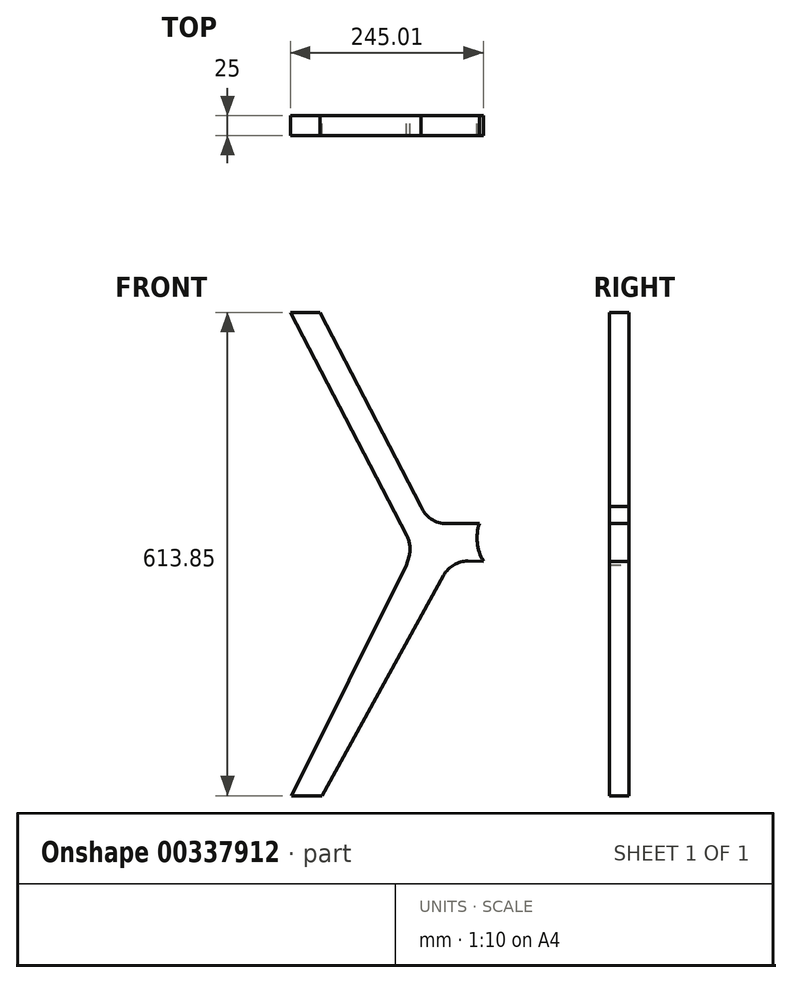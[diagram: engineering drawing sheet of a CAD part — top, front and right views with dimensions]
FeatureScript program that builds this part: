
annotation { "Feature Type Name" : "Feature", "Feature Type Description" : "" }
export const myFeature = defineFeature(function(context is Context, id is Id, definition is map)
    precondition{}
    {
        {
            var Q0;
            Q0=qCreatedBy(makeId("Front.planeOp"),FACE);
            var sketch = newSketch(context, id + "F0", { "sketchPlane" : qUnion([Q0])});
            skLineSegment(sketch, "E0.top", {"start": v(348.78, -158.15) * mm, "end": v(325.9, -158.15) * mm});
            skLineSegment(sketch, "E0.left", {"start": v(348.78, 219.3) * mm, "end": v(348.78, -158.15) * mm});
            skPoint(sketch, "E0.middle", {"position": v(0, 0) * mm});
            skLineSegment(sketch, "E1", {"start": v(-310.5, 344.83) * mm, "end": v(-363.6, 344.83) * mm});
            skFitSpline(sketch, "E2", {"points": [v(-350.67, 344.83) * mm, v(347.35, 254.73) * mm, v(923.32, -91.46) * mm, v(911.37, -154.4) * mm, v(869.65, -185.3) * mm], "startDerivative": vector(1663.46, -7.35) * mm, "endDerivative": vector(-3077.7, -870.32) * mm});
            skLineSegment(sketch, "E3", {"start": v(348.78, 219.3) * mm, "end": v(347.5, 251.23) * mm});
            skLineSegment(sketch, "E4.0", {"start": v(280.23, 190.93) * mm, "end": v(-218.88, 187.87) * mm});
            skPoint(sketch, "E5.newPointA", {"position": v(-350, 535) * mm});
            skLineSegment(sketch, "E6", {"start": v(-318.8, 187.25) * mm, "end": v(-458.7, 455.7) * mm});
            skLineSegment(sketch, "E7", {"start": v(-311.32, 135.27) * mm, "end": v(-457.28, -158.15) * mm});
            skLineSegment(sketch, "E8", {"start": v(-418.69, -158.15) * mm, "end": v(-457.28, -158.15) * mm});
            skArc(sketch, "E9", {"start": v(-218.88, 187.87) * mm, "mid": v(-221.35, 163.28) * mm, "end": v(-213.7, 139.78) * mm});
            skLineSegment(sketch, "E10.trimOffspring", {"start": v(326.04, -158.15) * mm, "end": v(326.04, -159.41) * mm});
            skLineSegment(sketch, "E11", {"start": v(-318.8, 187.25) * mm, "end": v(-310.8, 171.92) * mm});
            skLineSegment(sketch, "E12", {"start": v(-311.32, 135.27) * mm, "end": v(-308.21, 146.05) * mm});
            skArc(sketch, "E13.filletArc", {"start": v(-308.21, 146.05) * mm, "mid": v(-307.02, 159.24) * mm, "end": v(-310.8, 171.92) * mm});
            skLineSegment(sketch, "E14.filletArc", {"start": v(279.23, 184.4) * mm, "end": v(279.23, 184.4) * mm});
            skLineSegment(sketch, "E15", {"start": v(280.23, 190.93) * mm, "end": v(300.92, 190.93) * mm});
            skLineSegment(sketch, "E16.trimOffspring", {"start": v(325.9, -158.15) * mm, "end": v(326.04, -159.41) * mm});
            skLineSegment(sketch, "E17", {"start": v(-287.9, 78.75) * mm, "end": v(-418.69, -158.15) * mm});
            skArc(sketch, "E18.trimOffspring", {"start": v(299.4, 190.93) * mm, "mid": v(299.33, 190.97) * mm, "end": v(299.25, 191) * mm});
            skArc(sketch, "E19.0", {"start": v(307.52, 136.2) * mm, "mid": v(309.15, 164.16) * mm, "end": v(300.92, 190.93) * mm});
            skLineSegment(sketch, "E20", {"start": v(294.6, 136.3) * mm, "end": v(-233.24, 139.91) * mm});
            skArc(sketch, "E21.filletArc", {"start": v(314.46, 116.85) * mm, "mid": v(308.46, 130.58) * mm, "end": v(294.6, 136.3) * mm});
            skLineSegment(sketch, "E22.0", {"start": v(-292.9, 209.2) * mm, "end": v(-421.38, 455.7) * mm});
            skLineSegment(sketch, "E23", {"start": v(-194.49, 188.02) * mm, "end": v(-260.36, 187.61) * mm});
            skArc(sketch, "E24.filletArc", {"start": v(-292.9, 209.2) * mm, "mid": v(-279.92, 193.44) * mm, "end": v(-260.36, 187.61) * mm});
            skLineSegment(sketch, "E25", {"start": v(-457.28, -158.15) * mm, "end": v(348.78, -158.15) * mm, "construction": true});
            skLineSegment(sketch, "E26", {"start": v(-458.7, 455.7) * mm, "end": v(-421.38, 455.7) * mm});
            skLineSegment(sketch, "E27", {"start": v(-297.94, 60.56) * mm, "end": v(-264.12, 121.83) * mm});
            skArc(sketch, "E28.filletArc", {"start": v(-233.24, 139.91) * mm, "mid": v(-251.17, 135.12) * mm, "end": v(-264.12, 121.83) * mm});
            skLineSegment(sketch, "E29", {"start": v(314.46, 116.85) * mm, "end": v(323.78, -158.15) * mm});
            skLineSegment(sketch, "E30", {"start": v(323.78, -158.15) * mm, "end": v(348.78, -158.15) * mm});
            skLineSegment(sketch, "E31", {"start": v(300.92, 190.93) * mm, "end": v(309.64, 190.93) * mm});
            skArc(sketch, "E32.filletArc", {"start": v(309.64, 190.93) * mm, "mid": v(323.78, 196.79) * mm, "end": v(329.64, 210.93) * mm});
            skLineSegment(sketch, "E33", {"start": v(347.5, 251.23) * mm, "end": v(347.5, 286.23) * mm});
            skLineSegment(sketch, "E34", {"start": v(-363.6, 379.83) * mm, "end": v(-381.83, 379.83) * mm});
            skFitSpline(sketch, "E35", {"points": [v(-381.83, 379.83) * mm, v(347.5, 286.23) * mm, v(695.3, 144.82) * mm], "startDerivative": vector(1371.77, -108.32) * mm, "endDerivative": vector(747.87, -376.57) * mm});
            skLineSegment(sketch, "E36", {"start": v(329.64, 210.93) * mm, "end": v(329.64, 260.32) * mm});
            skLineSegment(sketch, "E37", {"start": v(347.5, 286.23) * mm, "end": v(329.64, 260.32) * mm});
            skLineSegment(sketch, "E38", {"start": v(307.52, 136.2) * mm, "end": v(294.6, 136.3) * mm});
            skSolve(sketch);
        }
        {
            var Q0;
            Q0=makeQuery(id+"F0.imprint","IMPRINT",FACE,{"disambiguationData":[TD([[makeQuery(id+"F0.imprint","IMPRINT",EDGE,{"derivedFrom":sQuery(id+"F0.wireOp",EDGE,"E6")}),-1.0]])]});
            var sketch = newSketch(context, id + "F1", { "sketchPlane" : qUnion([Q0])});
            skLineSegment(sketch, "E39.0", {"start": v(-287.9, 78.75) * mm, "end": v(-418.69, -158.15) * mm});
            skLineSegment(sketch, "E39.1", {"start": v(-311.32, 135.27) * mm, "end": v(-457.28, -158.15) * mm});
            skLineSegment(sketch, "E39.2", {"start": v(-318.8, 187.25) * mm, "end": v(-458.7, 455.7) * mm});
            skLineSegment(sketch, "E39.3", {"start": v(-292.9, 209.2) * mm, "end": v(-421.38, 455.7) * mm});
            skLineSegment(sketch, "E39.4", {"start": v(-218.88, 187.87) * mm, "end": v(-260.36, 187.61) * mm});
            skArc(sketch, "E39.5.0", {"start": v(-213.7, 139.78) * mm, "mid": v(-221.35, 163.28) * mm, "end": v(-218.88, 187.87) * mm});
            skLineSegment(sketch, "E39.5.1", {"start": v(-218.88, 187.87) * mm, "end": v(-260.36, 187.61) * mm});
            skArc(sketch, "E39.5.2", {"start": v(-260.36, 187.61) * mm, "mid": v(-279.92, 193.44) * mm, "end": v(-292.9, 209.2) * mm});
            skLineSegment(sketch, "E39.5.3", {"start": v(-292.9, 209.2) * mm, "end": v(-363.6, 344.83) * mm});
            skLineSegment(sketch, "E39.5.4", {"start": v(-363.6, 344.83) * mm, "end": v(-381.83, 379.83) * mm});
            skLineSegment(sketch, "E39.5.5", {"start": v(-381.83, 379.83) * mm, "end": v(-421.38, 455.7) * mm});
            skLineSegment(sketch, "E39.5.6", {"start": v(-421.38, 455.7) * mm, "end": v(-458.7, 455.7) * mm});
            skLineSegment(sketch, "E39.5.7", {"start": v(-458.7, 455.7) * mm, "end": v(-318.8, 187.25) * mm});
            skLineSegment(sketch, "E39.5.8", {"start": v(-318.8, 187.25) * mm, "end": v(-310.8, 171.92) * mm});
            skArc(sketch, "E39.5.9", {"start": v(-310.8, 171.92) * mm, "mid": v(-307.02, 159.24) * mm, "end": v(-308.21, 146.05) * mm});
            skLineSegment(sketch, "E39.5.10", {"start": v(-308.21, 146.05) * mm, "end": v(-311.32, 135.27) * mm});
            skLineSegment(sketch, "E39.5.11", {"start": v(-311.32, 135.27) * mm, "end": v(-457.28, -158.15) * mm});
            skLineSegment(sketch, "E39.5.12", {"start": v(-457.28, -158.15) * mm, "end": v(-418.69, -158.15) * mm});
            skLineSegment(sketch, "E39.5.13", {"start": v(-418.69, -158.15) * mm, "end": v(-297.94, 60.56) * mm});
            skLineSegment(sketch, "E39.5.14", {"start": v(-297.94, 60.56) * mm, "end": v(-264.12, 121.83) * mm});
            skArc(sketch, "E39.5.15", {"start": v(-264.12, 121.83) * mm, "mid": v(-251.17, 135.12) * mm, "end": v(-233.24, 139.91) * mm});
            skLineSegment(sketch, "E39.5.16", {"start": v(-233.24, 139.91) * mm, "end": v(-213.7, 139.78) * mm});
            skPoint(sketch, "E39.6", {"position": v(-221.35, 163.28) * mm});
            skPoint(sketch, "E40.orphan", {"position": v(-194.49, 188.02) * mm});
            skSolve(sketch);
        }
        {
            var Q0;
            Q0 = qSketchRegion(id + "F1", true);
            extrude(context, id + "F2", {"entities" : qUnion([Q0]), "depth" : 25 * mm});
        }
    });
